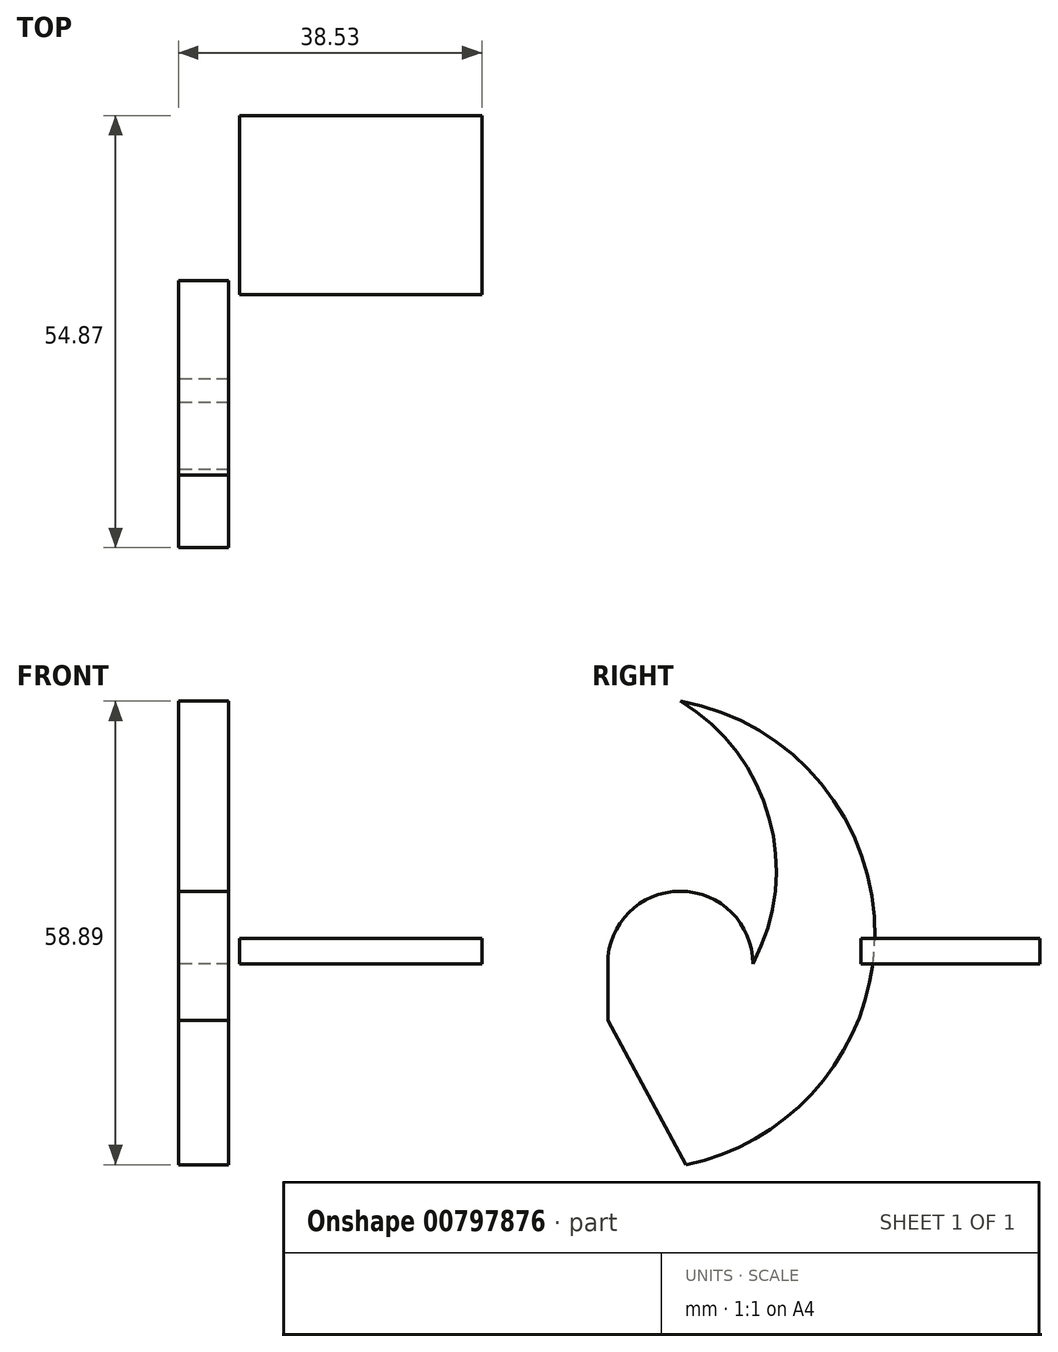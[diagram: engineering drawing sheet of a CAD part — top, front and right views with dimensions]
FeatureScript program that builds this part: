
annotation { "Feature Type Name" : "Feature", "Feature Type Description" : "" }
export const myFeature = defineFeature(function(context is Context, id is Id, definition is map)
    precondition{}
    {
        {
            var Q0;
            Q0=qCreatedBy(makeId("Top.planeOp"),FACE);
            var sketch = newSketch(context, id + "F0", { "sketchPlane" : qUnion([Q0])});
            skLineSegment(sketch, "E0", {"start": v(-72.16, 73.88) * mm, "end": v(-47.75, 13.99) * mm});
            skLineSegment(sketch, "E1", {"start": v(-47.75, 13.99) * mm, "end": v(-20.97, 38.3) * mm});
            skLineSegment(sketch, "E2", {"start": v(-20.97, 38.3) * mm, "end": v(0, 0) * mm});
            skLineSegment(sketch, "E3", {"start": v(0, 0) * mm, "end": v(31, 6.19) * mm});
            skLineSegment(sketch, "E4.bottom", {"start": v(38.53, -28.43) * mm, "end": v(7.76, -28.43) * mm});
            skLineSegment(sketch, "E4.top", {"start": v(38.53, -5.72) * mm, "end": v(7.76, -5.72) * mm});
            skLineSegment(sketch, "E4.left", {"start": v(38.53, -28.43) * mm, "end": v(38.53, -5.72) * mm});
            skLineSegment(sketch, "E4.right", {"start": v(7.76, -28.43) * mm, "end": v(7.76, -5.72) * mm});
            skSolve(sketch);
        }
        {
            var Q0;
            Q0 = qSketchRegion(id + "F0", true);
            extrude(context, id + "F1", {"entities" : qUnion([Q0]), "depth" : 3.22 * mm, "offsetDistance" : 25.4 * mm});
        }
        {
            var Q0;
            Q0=qCreatedBy(makeId("Right.planeOp"),FACE);
            var sketch = newSketch(context, id + "F2", { "sketchPlane" : qUnion([Q0])});
            skLineSegment(sketch, "E5", {"start": v(-50.65, -25.52) * mm, "end": v(-60.6, -7.17) * mm});
            skLineSegment(sketch, "E6", {"start": v(-60.6, -7.17) * mm, "end": v(-60.6, 0) * mm});
            skArc(sketch, "E7", {"start": v(-42.17, 0) * mm, "mid": v(-51.38, 9.21) * mm, "end": v(-60.6, 0) * mm});
            skArc(sketch, "E8", {"start": v(-50.65, -25.52) * mm, "mid": v(-26.67, 4.22) * mm, "end": v(-51.38, 33.37) * mm});
            skPoint(sketch, "E8.endSnap0", {"position": v(-51.38, 9.21) * mm});
            skArc(sketch, "E9", {"start": v(-42.17, 0) * mm, "mid": v(-40.09, 18.53) * mm, "end": v(-51.38, 33.37) * mm});
            skSolve(sketch);
        }
        {
            var Q0;
            Q0=makeQuery(id+"F2.imprint","IMPRINT",FACE,{"disambiguationData":[TD([[makeQuery(id+"F2.imprint","IMPRINT",EDGE,{"derivedFrom":sQuery(id+"F2.wireOp",EDGE,"E5")}),-1.0]])]});
            extrude(context, id + "F3", {"entities" : qUnion([Q0]), "depth" : 6.35 * mm, "offsetDistance" : 25.4 * mm});
        }
    });
